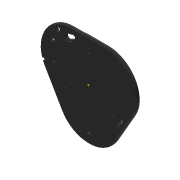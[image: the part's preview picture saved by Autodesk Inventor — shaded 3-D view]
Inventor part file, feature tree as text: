
AUTODESK INVENTOR PART (.ipt)
format: ipt  version: 2016 (Build 200138000, 138)  size: 395,264 bytes
history: native  units: mm
features: reference x45, sketch x17, extrude x15, thread x4, hole x3, pattern_circular x2
ambient origin geometry x8: Origin, YZ Plane, XZ Plane, XY Plane, X Axis, Y Axis, Z Axis, Center Point
bodies: Body1 (feature_tree)
feature tree (86):
  extrude  "Extrusion2"  Depth=10.0mm TaperAngle=0.0deg
  extrude  "Extrusion3"  Depth=10.0mm TaperAngle=0.0deg
  pattern_circular  "Circular Pattern1"  Count=3 Angle=360.0deg
  extrude  "Extrusion5"  Depth=10.0mm TaperAngle=0.0deg
  extrude  "Extrusion6"  Depth=3.3mm
  extrude  "Extrusion9"  Depth=3.3mm
  pattern_circular  "Circular Pattern2"  [2 undecoded]
  extrude  "Extrusion10"  Depth=10.0mm TaperAngle=0.0deg
  extrude  "Extrusion11"  Depth=10.0mm TaperAngle=0.0deg
  extrude  "Extrusion12"  Depth=10.0mm TaperAngle=0.0deg
  thread  "Thread1"  [1 undecoded]
  thread  "Thread2"  [1 undecoded]
  thread  "Thread3"  [1 undecoded]
  thread  "Thread4"  [1 undecoded]
  sketch  "Sketch15"  dims[d47=3.3mm d48=3.3mm]
  extrude  "Extrusion14"  Depth=3.0mm
  extrude  "Extrusion15"  Depth=10.0mm TaperAngle=0.0deg
  hole  "Hole1"  [1 undecoded]
  extrude  "Extrusion19"  Depth=3.1mm TaperAngle=0.0deg
  extrude  "Extrusion20"  Depth=3.5mm
  extrude  "Extrusion21"  Depth=16.7mm
  hole  "Hole2"  [1 undecoded]
  extrude  "Extrusion22"  Depth=10.0mm
  hole  "Hole3"  [1 undecoded]
  extrude  "Extrusion23"  Depth=10.0mm
  sketch  "Sketch3"  dims[d9=10.0mm d10=0.0mm d11=10.0mm d12=0.0mm]
  reference  "Reference16"
  reference  "Reference17"
  reference  "Reference18"
  reference  "Reference19"
  reference  "Reference20"
  reference  "Reference21"
  reference  "Reference22"
  reference  "Reference23"
  reference  "Reference24"
  reference  "Reference25"
  reference  "Reference26"
  reference  "Reference27"
  reference  "Reference28"
  reference  "Reference29"
  reference  "Reference30"
  reference  "Reference31"
  sketch  "Sketch4"  dims[d13=30.0mm d14=360.0deg d23=10.0mm d24=0.0mm]
  reference  "Reference32"
  reference  "Reference33"
  reference  "Reference34"
  reference  "Reference35"
  reference  "Reference36"
  reference  "Reference37"
  reference  "Reference38"
  reference  "Reference39"
  reference  "Reference40"
  reference  "Reference41"
  sketch  "Sketch8"  dims[d25=0.5mm]
  reference  "Reference46"
  reference  "Reference47"
  reference  "Reference48"
  reference  "Reference49"
  sketch  "Sketch11"  dims[d26=0.5mm]
  sketch  "Sketch12"  dims[d29=6.3mm d30=0.0mm]
  reference  "Reference50"
  reference  "Reference51"
  sketch  "Sketch13"  dims[d38=10.0mm d39=0.0mm d40=30.0mm d41=360.0deg]
  sketch  "Sketch14"  dims[d43=3.0mm d44=0.0mm d45=10.0mm d46=0.0mm]
  reference  "Reference52"
  reference  "Reference53"
  reference  "Reference54"
  reference  "Reference55"
  sketch  "Sketch16"  dims[d49=3.3mm d50=3.3mm]
  reference  "Reference57"
  reference  "Reference58"
  reference  "Reference59"
  reference  "Reference60"
  sketch  "Sketch17"  dims[d51=5.8mm]
  sketch  "Sketch20"  dims[d52=5.8mm]
  reference  "Reference67"
  reference  "Reference68"
  reference  "Reference69"
  reference  "Reference70"
  reference  "Reference71"
  sketch  "Sketch22"  dims[d53=5.8mm]
  sketch  "Sketch23"  dims[d54=5.8mm]
  sketch  "Sketch24"  dims[d55=6.0mm]
  sketch  "Sketch25"  dims[d56=32.5mm]
  sketch  "Sketch26"  dims[d57=6.0mm]
  sketch  "Sketch27"  dims[d58=32.5mm d59=10.0mm d60=0.0mm d61=10.0mm d62=0.0mm d63=10.0mm d64=0.0mm d65=10.0mm d66=0.0mm d67=10.0mm d68=0.0mm d69=3.0mm d70=3.0mm d71=3.0mm d72=3.0mm d83=10.0mm d84=0.0mm d85=5.0mm d86=3.1mm d87=0.0mm d89=3.5mm d90=16.7mm d91=12.0mm d92=12.0mm d108=2.459mm d109=7.0mm d110=4.0mm d111=2.0mm d112=90.0deg d113=8.5mm d114=20.594885mm d118=18.0mm d119=89.0mm d120=53.0mm d121=12.0mm d122=25.0mm d123=70.0mm d124=10.0mm d125=0.0mm d126=10.0mm d127=20.0mm d128=20.0mm d129=0.0mm d130=8.5mm d131=110.0mm d132=30.0mm d134=360.0deg d136=10.0mm d137=0.0mm d148=3.242mm d149=7.0mm d150=4.0mm d151=2.0mm d152=90.0deg d153=8.5mm d154=20.594885mm d155=6.6mm d156=0.4mm d157=9.0mm d158=11.0mm d159=10.0mm d160=0.0mm d161=2.459mm d162=6.0mm d163=4.0mm d164=2.0mm d165=90.0deg d166=8.0mm d167=20.594885mm d168=10.0mm d169=0.0mm]
note: 9 required parameter values undecoded (feature->parameter linkage not recoverable at this tier; creation-order binding heuristic only, values carry confidence <= 0.55)
